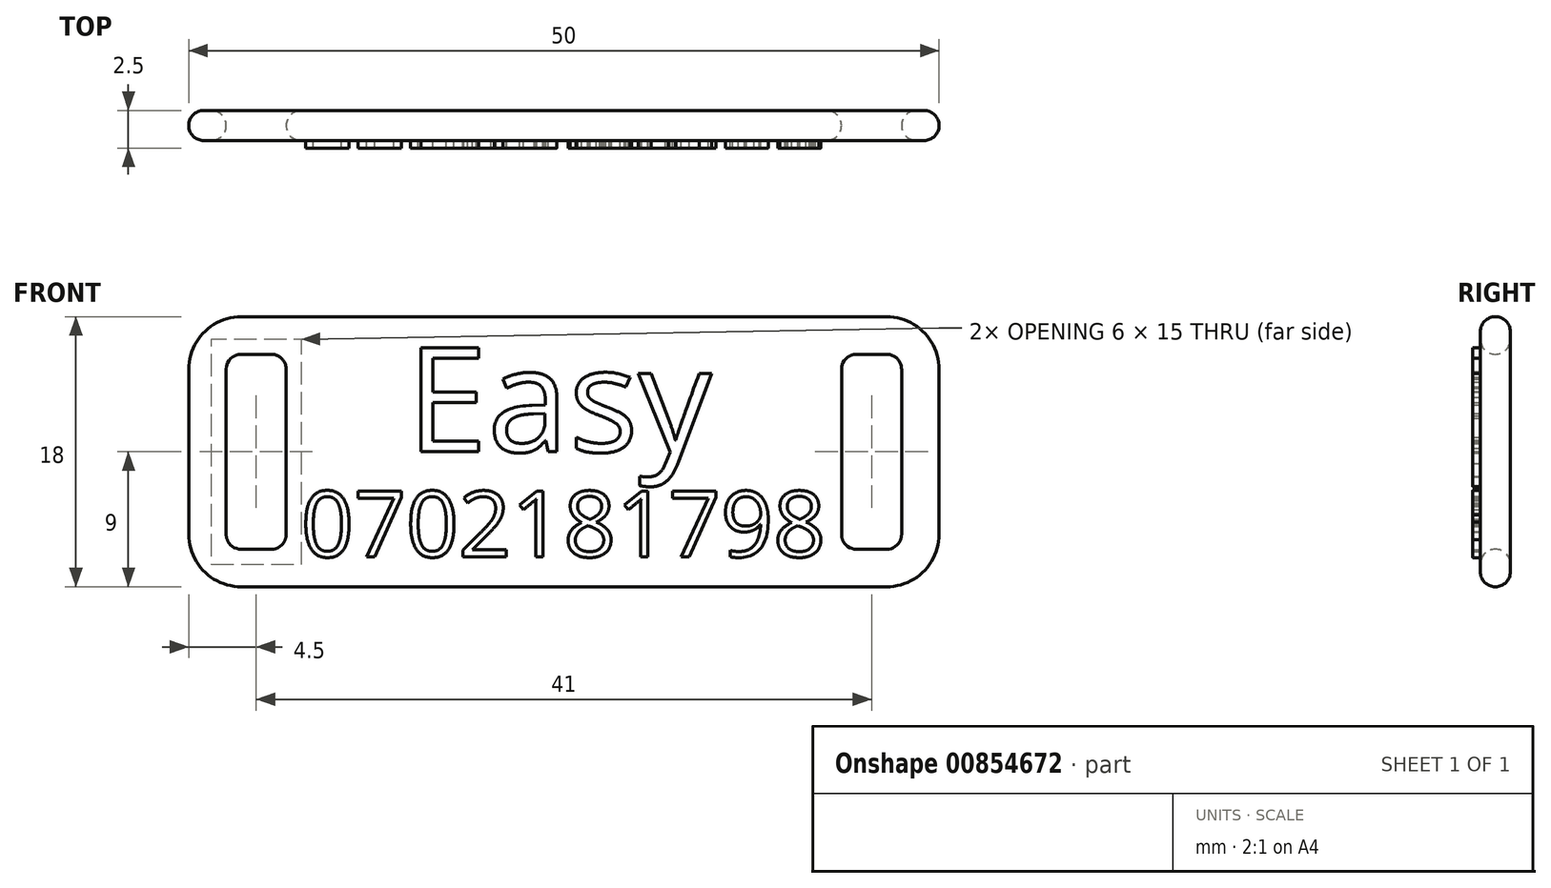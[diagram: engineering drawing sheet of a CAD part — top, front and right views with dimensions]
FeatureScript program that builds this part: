
annotation { "Feature Type Name" : "Feature", "Feature Type Description" : "" }
export const myFeature = defineFeature(function(context is Context, id is Id, definition is map)
    precondition{}
    {
        {
            var Q0;
            Q0=qCreatedBy(makeId("Front.planeOp"),FACE);
            var sketch = newSketch(context, id + "F0", { "sketchPlane" : qUnion([Q0])});
            skLineSegment(sketch, "E0.bottom", {"start": v(-25, 9) * mm, "end": v(25, 9) * mm});
            skLineSegment(sketch, "E0.top", {"start": v(-25, -9) * mm, "end": v(25, -9) * mm});
            skLineSegment(sketch, "E0.left", {"start": v(-25, 9) * mm, "end": v(-25, -9) * mm});
            skLineSegment(sketch, "E0.right", {"start": v(25, 9) * mm, "end": v(25, -9) * mm});
            skPoint(sketch, "E0.middle", {"position": v(0, 0) * mm});
            skLineSegment(sketch, "E1.bottom", {"start": v(-18.5, 6.5) * mm, "end": v(-22.5, 6.5) * mm});
            skLineSegment(sketch, "E1.top", {"start": v(-18.5, -6.5) * mm, "end": v(-22.5, -6.5) * mm});
            skLineSegment(sketch, "E1.left", {"start": v(-18.5, 6.5) * mm, "end": v(-18.5, -6.5) * mm});
            skLineSegment(sketch, "E1.right", {"start": v(-22.5, 6.5) * mm, "end": v(-22.5, -6.5) * mm});
            skPoint(sketch, "E1.middle", {"position": v(-20.5, 0) * mm});
            skPoint(sketch, "E2.MirrorP", {"position": v(20.5, 0) * mm});
            skLineSegment(sketch, "E3.MirrorCS", {"start": v(18.5, 6.5) * mm, "end": v(18.5, -6.5) * mm});
            skLineSegment(sketch, "E4.MirrorCS", {"start": v(18.5, 6.5) * mm, "end": v(22.5, 6.5) * mm});
            skLineSegment(sketch, "E5.MirrorCS", {"start": v(18.5, -6.5) * mm, "end": v(22.5, -6.5) * mm});
            skLineSegment(sketch, "E6.MirrorCS", {"start": v(22.5, 6.5) * mm, "end": v(22.5, -6.5) * mm});
            skSolve(sketch);
        }
        {
            var Q0;
            Q0=makeQuery(id+"F0.imprint","IMPRINT",FACE,{"disambiguationData":[TD([[makeQuery(id+"F0.imprint","IMPRINT",EDGE,{"derivedFrom":sQuery(id+"F0.wireOp",EDGE,"E0.bottom")}),-1.0]])]});
            extrude(context, id + "F1", {"entities" : qUnion([Q0]), "depth" : 2 * mm, "offsetDistance" : 25 * mm});
        }
        {
            var Q0;
            Q0=makeQuery(id+"F1.opExtrude","CAP_FACE",FACE,{"disambiguationData":[OSD([sQuery(id+"F0.wireOp",EDGE,"E0.bottom"),sQuery(id+"F0.wireOp",EDGE,"E0.top"),sQuery(id+"F0.wireOp",EDGE,"E0.left"),sQuery(id+"F0.wireOp",EDGE,"E0.right"),sQuery(id+"F0.wireOp",EDGE,"E1.bottom"),sQuery(id+"F0.wireOp",EDGE,"E1.top"),sQuery(id+"F0.wireOp",EDGE,"E1.left"),sQuery(id+"F0.wireOp",EDGE,"E1.right"),sQuery(id+"F0.wireOp",EDGE,"E3.MirrorCS"),sQuery(id+"F0.wireOp",EDGE,"E4.MirrorCS"),sQuery(id+"F0.wireOp",EDGE,"E5.MirrorCS"),sQuery(id+"F0.wireOp",EDGE,"E6.MirrorCS")])],"isStart":false});
            var sketch = newSketch(context, id + "F2", { "sketchPlane" : qUnion([Q0])});
            skText(sketch, "E7", { "text": "Easy", "fontName": "OpenSans-Regular.ttf"});
            const initialGuessF2  = {"E7": [-0.01049, 0, 1, 0, 0.007]};
            skSetInitialGuess(sketch, initialGuessF2);
            skSolve(sketch);
        }
        {
            var Q0;
            {var subQ0=sQuery(id+"F0.wireOp",EDGE,"E3.MirrorCS");var subQ1=sQuery(id+"F0.wireOp",EDGE,"E1.right");var subQ2=sQuery(id+"F0.wireOp",EDGE,"E1.left");var subQ3=sQuery(id+"F0.wireOp",EDGE,"E1.top");var subQ4=sQuery(id+"F0.wireOp",EDGE,"E1.bottom");var subQ5=sQuery(id+"F0.wireOp",EDGE,"E4.MirrorCS");var subQ6=sQuery(id+"F0.wireOp",EDGE,"E0.bottom");var subQ7=sQuery(id+"F0.wireOp",EDGE,"E0.right");var subQ8=sQuery(id+"F0.wireOp",EDGE,"E0.top");var subQ9=sQuery(id+"F0.wireOp",EDGE,"E0.left");var subQ10=sQuery(id+"F0.wireOp",EDGE,"E5.MirrorCS");var subQ11=sQuery(id+"F0.wireOp",EDGE,"E6.MirrorCS");Q0=makeQuery(id+"F4.boolean.opBoolean","SPLIT",FACE,{"disambiguationData":[TD([makeQuery(id+"F1.opExtrude","SWEPT_FACE",FACE,{"disambiguationData":[OSD([subQ6])]})])],"derivedFrom":makeQuery(id+"F1.opExtrude","CAP_FACE",FACE,{"disambiguationData":[OSD([subQ6,subQ8,subQ9,subQ7,subQ4,subQ3,subQ2,subQ1,subQ0,subQ5,subQ10,subQ11])],"isStart":false})});}
            var sketch = newSketch(context, id + "F3", { "sketchPlane" : qUnion([Q0])});
            skText(sketch, "E8", { "text": "0702181798", "fontName": "OpenSans-Regular.ttf"});
            const initialGuessF3  = {"E8": [-0.0175, -0.007, 1, 0, 0.0044]};
            skSetInitialGuess(sketch, initialGuessF3);
            skSolve(sketch);
        }
        {
            var Q0;
            Q0 = qSketchRegion(id + "F2", true);
            var Q1;
            Q1 = qSketchRegion(id + "F3", true);
            extrude(context, id + "F4", {"entities" : qUnion([Q0, Q1]), "operationType" : NewBodyOperationType.ADD, "depth" : .5 * mm, "offsetDistance" : 25 * mm});
        }
        {
            var Q0;
            Q0=makeQuery(id+"F1.opExtrude","SWEPT_EDGE",EDGE,{"disambiguationData":[OSD([sQuery(id+"F0.wireOp",EDGE,"E1.bottom"),sQuery(id+"F0.wireOp",EDGE,"E1.left")])]});
            var Q1;
            Q1=makeQuery(id+"F1.opExtrude","SWEPT_EDGE",EDGE,{"disambiguationData":[OSD([sQuery(id+"F0.wireOp",EDGE,"E4.MirrorCS"),sQuery(id+"F0.wireOp",EDGE,"E6.MirrorCS")])]});
            var Q2;
            Q2=makeQuery(id+"F1.opExtrude","SWEPT_EDGE",EDGE,{"disambiguationData":[OSD([sQuery(id+"F0.wireOp",EDGE,"E1.bottom"),sQuery(id+"F0.wireOp",EDGE,"E1.right")])]});
            var Q3;
            Q3=makeQuery(id+"F1.opExtrude","SWEPT_EDGE",EDGE,{"disambiguationData":[OSD([sQuery(id+"F0.wireOp",EDGE,"E3.MirrorCS"),sQuery(id+"F0.wireOp",EDGE,"E4.MirrorCS")])]});
            var Q4;
            Q4=makeQuery(id+"F1.opExtrude","SWEPT_EDGE",EDGE,{"disambiguationData":[OSD([sQuery(id+"F0.wireOp",EDGE,"E5.MirrorCS"),sQuery(id+"F0.wireOp",EDGE,"E6.MirrorCS")])]});
            var Q5;
            Q5=makeQuery(id+"F1.opExtrude","SWEPT_EDGE",EDGE,{"disambiguationData":[OSD([sQuery(id+"F0.wireOp",EDGE,"E1.top"),sQuery(id+"F0.wireOp",EDGE,"E1.left")])]});
            var Q6;
            Q6=makeQuery(id+"F1.opExtrude","SWEPT_EDGE",EDGE,{"disambiguationData":[OSD([sQuery(id+"F0.wireOp",EDGE,"E1.top"),sQuery(id+"F0.wireOp",EDGE,"E1.right")])]});
            var Q7;
            Q7=makeQuery(id+"F1.opExtrude","SWEPT_EDGE",EDGE,{"disambiguationData":[OSD([sQuery(id+"F0.wireOp",EDGE,"E3.MirrorCS"),sQuery(id+"F0.wireOp",EDGE,"E5.MirrorCS")])]});
            fillet(context, id + "F5", {"entities" : qUnion([Q0, Q1, Q2, Q3, Q4, Q5, Q6, Q7]), "radius" : 1 * mm, "tangentPropagation" : true, "allowEdgeOverflow" : false});
        }
        {
            var Q0;
            Q0=makeQuery(id+"F1.opExtrude","SWEPT_EDGE",EDGE,{"disambiguationData":[OSD([sQuery(id+"F0.wireOp",EDGE,"E0.top"),sQuery(id+"F0.wireOp",EDGE,"E0.left")])]});
            var Q1;
            Q1=makeQuery(id+"F1.opExtrude","SWEPT_EDGE",EDGE,{"disambiguationData":[OSD([sQuery(id+"F0.wireOp",EDGE,"E0.bottom"),sQuery(id+"F0.wireOp",EDGE,"E0.left")])]});
            var Q2;
            Q2=makeQuery(id+"F1.opExtrude","SWEPT_EDGE",EDGE,{"disambiguationData":[OSD([sQuery(id+"F0.wireOp",EDGE,"E0.top"),sQuery(id+"F0.wireOp",EDGE,"E0.right")])]});
            var Q3;
            Q3=makeQuery(id+"F1.opExtrude","SWEPT_EDGE",EDGE,{"disambiguationData":[OSD([sQuery(id+"F0.wireOp",EDGE,"E0.bottom"),sQuery(id+"F0.wireOp",EDGE,"E0.right")])]});
            fillet(context, id + "F6", {"entities" : qUnion([Q0, Q1, Q2, Q3]), "radius" : 3.5 * mm, "tangentPropagation" : true, "allowEdgeOverflow" : false});
        }
        {
            var Q0;
            Q0=makeQuery(id+"F1.opExtrude","CAP_EDGE",EDGE,{"disambiguationData":[OSD([sQuery(id+"F0.wireOp",EDGE,"E0.top")])],"isStart":false});
            var Q1;
            Q1=makeQuery(id+"F1.opExtrude","CAP_EDGE",EDGE,{"disambiguationData":[OSD([sQuery(id+"F0.wireOp",EDGE,"E0.top")])],"isStart":true});
            fillet(context, id + "F7", {"entities" : qUnion([Q0, Q1]), "radius" : 1 * mm, "tangentPropagation" : true, "allowEdgeOverflow" : false});
        }
        {
            var Q0;
            Q0=makeQuery(id+"F1.opExtrude","CAP_EDGE",EDGE,{"disambiguationData":[OSD([sQuery(id+"F0.wireOp",EDGE,"E1.top")])],"isStart":false});
            var Q1;
            Q1=makeQuery(id+"F1.opExtrude","CAP_EDGE",EDGE,{"disambiguationData":[OSD([sQuery(id+"F0.wireOp",EDGE,"E1.top")])],"isStart":true});
            var Q2;
            Q2=makeQuery(id+"F1.opExtrude","CAP_EDGE",EDGE,{"disambiguationData":[OSD([sQuery(id+"F0.wireOp",EDGE,"E5.MirrorCS")])],"isStart":true});
            var Q3;
            Q3=makeQuery(id+"F1.opExtrude","CAP_EDGE",EDGE,{"disambiguationData":[OSD([sQuery(id+"F0.wireOp",EDGE,"E5.MirrorCS")])],"isStart":false});
            fillet(context, id + "F8", {"entities" : qUnion([Q0, Q1, Q2, Q3]), "radius" : 1 * mm, "tangentPropagation" : true, "allowEdgeOverflow" : false});
        }
    });
